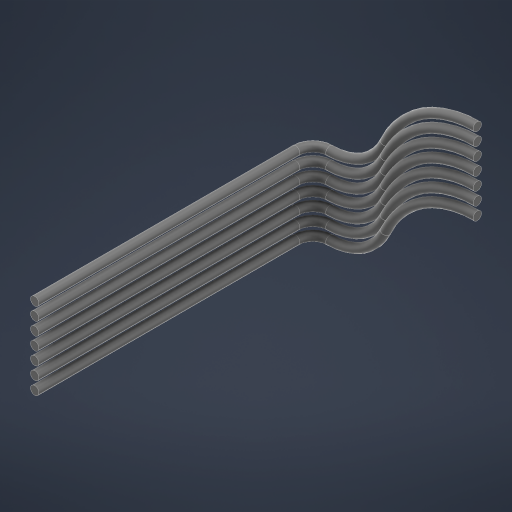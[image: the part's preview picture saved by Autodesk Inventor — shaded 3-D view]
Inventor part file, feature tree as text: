
AUTODESK INVENTOR PART (.ipt)
format: ipt  version: 2024.3 (Build 283343010, 343A)  size: 342,016 bytes
history: native  units: mm
features: sketch x3, plane x1, sweep x1, pattern_linear x1
ambient origin geometry x8: Origin, YZ Plane, XZ Plane, XY Plane, X Axis, Y Axis, Z Axis, Center Point
bodies: Volumenkörper1 (feature_tree)
feature tree (6):
  sketch  "Skizze1"  dims[d0=4.0mm d2=64.73mm]
  sketch  "Skizze2"  dims[d3=2.0mm]
  plane  "Arbeitsebene1"
  sweep  "Sweeping1"
  pattern_linear  "Rechteckige Anordnung1"  Spacing1=21.98mm  [1 undecoded]
  sketch  "Skizze3"  dims[d4=34.28mm d5=21.98mm d6=0.0mm d7=0.0mm d8=70.0mm d10=3.0mm]
note: 1 required parameter value undecoded (feature->parameter linkage not recoverable at this tier; creation-order binding heuristic only, values carry confidence <= 0.55)
